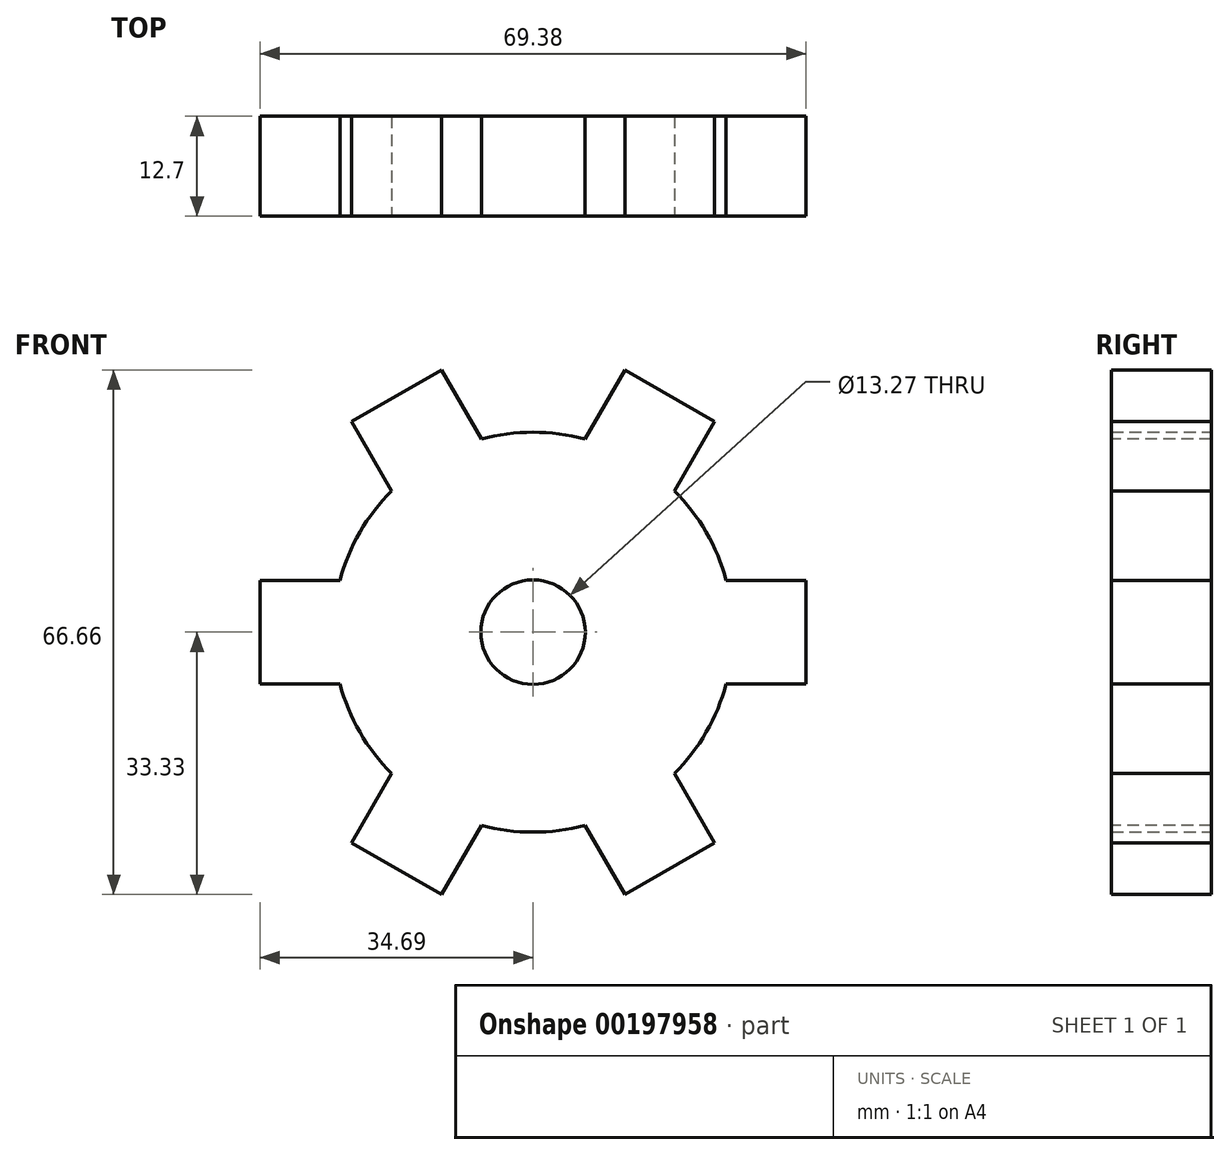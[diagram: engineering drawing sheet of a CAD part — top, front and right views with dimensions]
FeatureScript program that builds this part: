
annotation { "Feature Type Name" : "Feature", "Feature Type Description" : "" }
export const myFeature = defineFeature(function(context is Context, id is Id, definition is map)
    precondition{}
    {
        {
            var Q0;
            Q0=qCreatedBy(makeId("Front.planeOp"),FACE);
            var sketch = newSketch(context, id + "F0", { "sketchPlane" : qUnion([Q0])});
            skCircle(sketch, "E0", {"center": v(0, 0) * mm, "radius": 25.4 * mm});
            skSolve(sketch);
        }
        {
            var Q0;
            Q0 = qSketchRegion(id + "F0", true);
            extrude(context, id + "F1", {"entities" : qUnion([Q0]), "depth" : 12.7 * mm});
        }
        {
            var Q0;
            Q0=makeQuery(id+"F1.opExtrude","CAP_FACE",FACE,{"disambiguationData":[OSD([sQuery(id+"F0.wireOp",EDGE,"E0")])],"isStart":false});
            var sketch = newSketch(context, id + "F2", { "sketchPlane" : qUnion([Q0])});
            skLineSegment(sketch, "E1", {"start": v(0, 0) * mm, "end": v(25.4, 0) * mm});
            skLineSegment(sketch, "E2", {"start": v(0, 0) * mm, "end": v(24.53, -6.57) * mm});
            skLineSegment(sketch, "E3", {"start": v(0, 0) * mm, "end": v(24.53, 6.57) * mm});
            skLineSegment(sketch, "E4", {"start": v(24.53, 6.57) * mm, "end": v(24.53, -6.57) * mm});
            skLineSegment(sketch, "E5.0", {"start": v(34.7, 6.57) * mm, "end": v(34.7, -6.57) * mm});
            skLineSegment(sketch, "E6", {"start": v(34.7, 6.57) * mm, "end": v(24.53, 6.57) * mm});
            skLineSegment(sketch, "E7", {"start": v(34.7, -6.57) * mm, "end": v(24.53, -6.57) * mm});
            skSolve(sketch);
        }
        {
            var Q0;
            {var subQ0=sQuery(id+"F2.wireOp",EDGE,"E2");Q0=makeQuery(id+"F2.imprint","IMPRINT",FACE,{"disambiguationData":[TD([[makeQuery(id+"F2.imprint","IMPRINT",EDGE,{"derivedFrom":subQ0}),1.0]])]});}
            var Q1;
            {var subQ0=sQuery(id+"F2.wireOp",EDGE,"E3");Q1=makeQuery(id+"F2.imprint","IMPRINT",FACE,{"disambiguationData":[TD([[makeQuery(id+"F2.imprint","IMPRINT",EDGE,{"derivedFrom":subQ0}),-1.0]])]});}
            var Q2;
            {var subQ0=sQuery(id+"F2.wireOp",EDGE,"E1");var subQ1=makeQuery(id+"F1.opExtrude","CAP_EDGE",EDGE,{"disambiguationData":[OSD([sQuery(id+"F0.wireOp",EDGE,"E0")])],"isStart":false});var subQ2=makeQuery(id+"F2.imprint","INTERSECT",VERTEX,{"derivedFrom":[subQ1,subQ0]});Q2=makeQuery(id+"F2.imprint","IMPRINT",FACE,{"disambiguationData":[TD([[makeQuery(id+"F2.imprint","IMPRINT",EDGE,{"disambiguationData":[TD([[subQ2,1.0]])],"derivedFrom":subQ0}),1.0]])]});}
            var Q3;
            {var subQ0=sQuery(id+"F2.wireOp",EDGE,"E1");var subQ1=makeQuery(id+"F1.opExtrude","CAP_EDGE",EDGE,{"disambiguationData":[OSD([sQuery(id+"F0.wireOp",EDGE,"E0")])],"isStart":false});var subQ2=makeQuery(id+"F2.imprint","INTERSECT",VERTEX,{"derivedFrom":[subQ1,subQ0]});Q3=makeQuery(id+"F2.imprint","IMPRINT",FACE,{"disambiguationData":[TD([[makeQuery(id+"F2.imprint","IMPRINT",EDGE,{"disambiguationData":[TD([[subQ2,1.0]])],"derivedFrom":subQ0}),-1.0]])]});}
            var Q4;
            Q4=makeQuery(id+"F2.imprint","IMPRINT",FACE,{"disambiguationData":[TD([[makeQuery(id+"F2.imprint","IMPRINT",EDGE,{"derivedFrom":sQuery(id+"F2.wireOp",EDGE,"E5.0")}),-1.0]])]});
            extrude(context, id + "F3", {"entities" : qUnion([Q0, Q1, Q2, Q3, Q4]), "operationType" : NewBodyOperationType.ADD, "oppositeDirection" : true, "depth" : 12.7 * mm});
        }
        {
            var Q0;
            Q0=qCreatedBy(makeId("Right.planeOp"),FACE);
            var sketch = newSketch(context, id + "F4", { "sketchPlane" : qUnion([Q0])});
            skLineSegment(sketch, "E8", {"start": v(0, 0) * mm, "end": v(65.2, 0) * mm});
            skSolve(sketch);
        }
        {
            var Q0;
            Q0=makeQuery(id+"F1.opExtrude","SWEPT_BODY",BODY,{"disambiguationData":[OSD([sQuery(id+"F0.wireOp",EDGE,"E0")])]});
            var Q1;
            Q1=sQuery(id+"F4.wireOp",EDGE,"E8");
            circularPattern(context, id + "F5", {"operationType" : NewBodyOperationType.ADD, "entities" : qUnion([Q0]), "axis" : qUnion([Q1]), "angle" : 360 * degree, "instanceCount" : 6, "equalSpace" : true});
        }
        {
            var Q0;
            {var subQ0=makeQuery(id+"F3.boolean.opBoolean","MERGE",FACE,{"derivedFrom":[makeQuery(id+"F1.opExtrude","CAP_FACE",FACE,{"disambiguationData":[OSD([sQuery(id+"F0.wireOp",EDGE,"E0")])],"isStart":false}),makeQuery(id+"F3.opExtrude","CAP_FACE",FACE,{"disambiguationData":[OSD([sQuery(id+"F2.wireOp",EDGE,"E2"),sQuery(id+"F2.wireOp",EDGE,"E3"),sQuery(id+"F2.wireOp",EDGE,"E5.0"),sQuery(id+"F2.wireOp",EDGE,"E6"),sQuery(id+"F2.wireOp",EDGE,"E7")])],"isStart":true})]});Q0=makeQuery(id+"F5.boolean.opBoolean","MERGE",FACE,{"derivedFrom":[subQ0,makeQuery(id+"F5.opPattern","COPY",FACE,{"derivedFrom":subQ0,"instanceName":"1"}),makeQuery(id+"F5.opPattern","COPY",FACE,{"derivedFrom":subQ0,"instanceName":"2"}),makeQuery(id+"F5.opPattern","COPY",FACE,{"derivedFrom":subQ0,"instanceName":"3"}),makeQuery(id+"F5.opPattern","COPY",FACE,{"derivedFrom":subQ0,"instanceName":"4"}),makeQuery(id+"F5.opPattern","COPY",FACE,{"derivedFrom":subQ0,"instanceName":"5"})]});}
            var sketch = newSketch(context, id + "F6", { "sketchPlane" : qUnion([Q0])});
            skCircle(sketch, "E9", {"center": v(0, 0) * mm, "radius": 6.64 * mm});
            skSolve(sketch);
        }
        {
            var Q0;
            Q0 = qSketchRegion(id + "F6", true);
            extrude(context, id + "F7", {"entities" : qUnion([Q0]), "operationType" : NewBodyOperationType.REMOVE, "endBound" : BoundingType.THROUGH_ALL, "oppositeDirection" : true, "depth" : 25.4 * mm});
        }
    });
